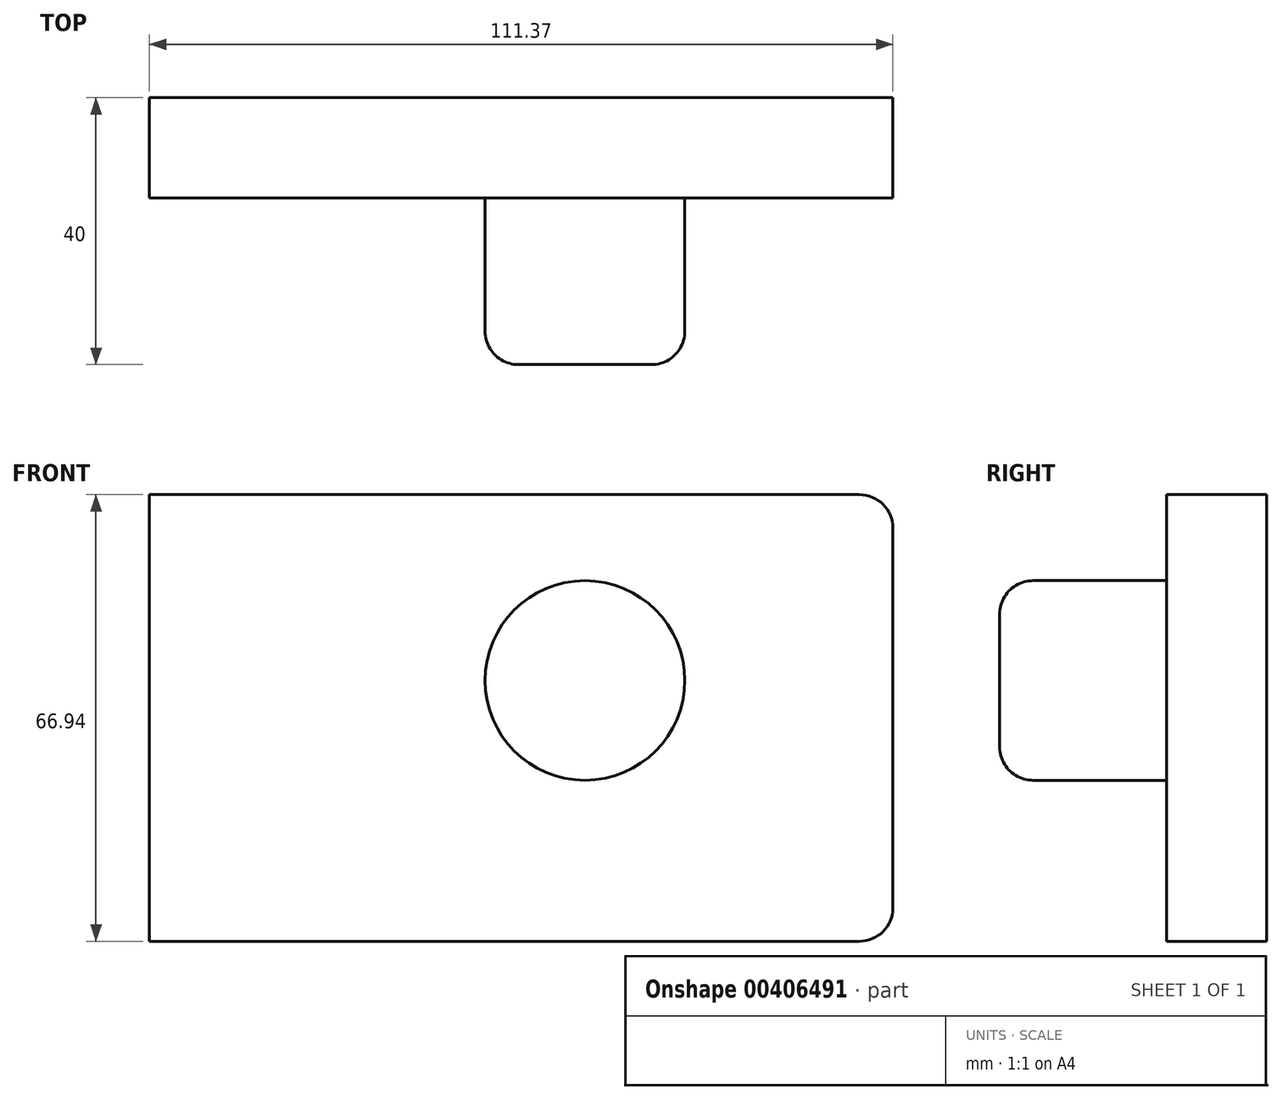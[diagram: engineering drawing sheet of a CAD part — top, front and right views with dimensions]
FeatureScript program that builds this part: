
annotation { "Feature Type Name" : "Feature", "Feature Type Description" : "" }
export const myFeature = defineFeature(function(context is Context, id is Id, definition is map)
    precondition{}
    {
        {
            var Q0;
            Q0=qCreatedBy(makeId("Front.planeOp"),FACE);
            var sketch = newSketch(context, id + "F0", { "sketchPlane" : qUnion([Q0])});
            skLineSegment(sketch, "E0.bottom", {"start": v(-57.03, 38.17) * mm, "end": v(54.34, 38.17) * mm});
            skLineSegment(sketch, "E0.top", {"start": v(-57.03, -28.77) * mm, "end": v(54.34, -28.77) * mm});
            skLineSegment(sketch, "E0.left", {"start": v(-57.03, 38.17) * mm, "end": v(-57.03, -28.77) * mm});
            skLineSegment(sketch, "E0.right", {"start": v(54.34, 38.17) * mm, "end": v(54.34, -28.77) * mm});
            skSolve(sketch);
        }
        {
            var Q0;
            Q0 = qSketchRegion(id + "F0", true);
            extrude(context, id + "F1", {"entities" : qUnion([Q0]), "depth" : 15 * mm});
        }
        {
            var Q0;
            Q0=makeQuery(id+"F1.opExtrude","CAP_FACE",FACE,{"disambiguationData":[OSD([sQuery(id+"F0.wireOp",EDGE,"E0.bottom"),sQuery(id+"F0.wireOp",EDGE,"E0.top"),sQuery(id+"F0.wireOp",EDGE,"E0.left"),sQuery(id+"F0.wireOp",EDGE,"E0.right")])],"isStart":false});
            var sketch = newSketch(context, id + "F2", { "sketchPlane" : qUnion([Q0])});
            skCircle(sketch, "E1", {"center": v(8.21, 10.32) * mm, "radius": 14.96 * mm});
            skSolve(sketch);
        }
        {
            var Q0;
            Q0 = qSketchRegion(id + "F2", true);
            extrude(context, id + "F3", {"entities" : qUnion([Q0]), "operationType" : NewBodyOperationType.ADD, "depth" : 25 * mm});
        }
        {
            var Q0;
            Q0=makeQuery(id+"F1.opExtrude","SWEPT_EDGE",EDGE,{"disambiguationData":[OSD([sQuery(id+"F0.wireOp",EDGE,"E0.bottom"),sQuery(id+"F0.wireOp",EDGE,"E0.right")])]});
            var Q1;
            Q1=makeQuery(id+"F1.opExtrude","SWEPT_EDGE",EDGE,{"disambiguationData":[OSD([sQuery(id+"F0.wireOp",EDGE,"E0.top"),sQuery(id+"F0.wireOp",EDGE,"E0.right")])]});
            var Q2;
            Q2=makeQuery(id+"F3.opExtrude","CAP_EDGE",EDGE,{"disambiguationData":[OSD([sQuery(id+"F2.wireOp",EDGE,"E1")])],"isStart":false});
            fillet(context, id + "F4", {"entities" : qUnion([Q0, Q1, Q2]), "radius" : 5 * mm, "tangentPropagation" : true, "allowEdgeOverflow" : false});
        }
    });
